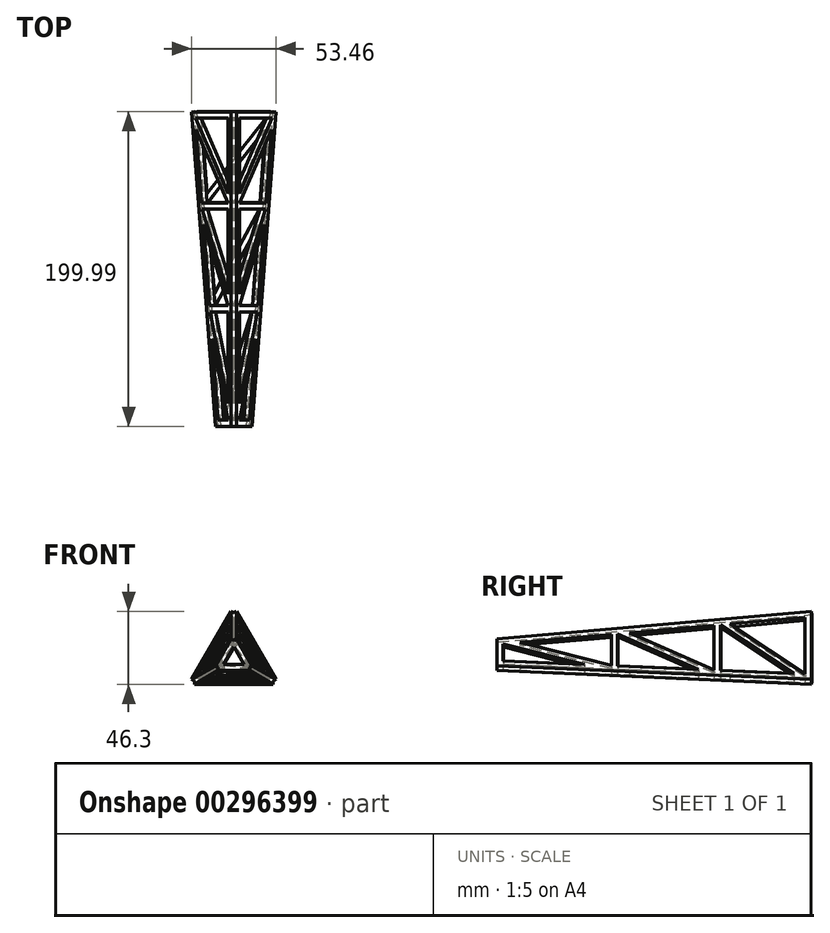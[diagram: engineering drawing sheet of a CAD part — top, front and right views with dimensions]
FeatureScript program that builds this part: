
annotation { "Feature Type Name" : "Feature", "Feature Type Description" : "" }
export const myFeature = defineFeature(function(context is Context, id is Id, definition is map)
    precondition{}
    {
        {
            assignVariable(context, id + "F0", {"name" : "thick", "anyValue" : 4});
        }
        {
            assignVariable(context, id + "F1", {"name" : "base", "anyValue" : 50});
        }
        {
            assignVariable(context, id + "F2", {"name" : "end", "anyValue" : 20});
        }
        {
            assignVariable(context, id + "F3", {"name" : "angleIn", "anyValue" : getVariable(context, 'base') / getVariable(context, 'end')});
        }
        {
            var Q0;
            Q0=qCreatedBy(makeId("Top.planeOp"),FACE);
            var sketch = newSketch(context, id + "F4", { "sketchPlane" : qUnion([Q0])});
            skLineSegment(sketch, "E0", {"start": v(0, 37.85) * mm, "end": v(0, -238.88) * mm, "construction": true});
            skSolve(sketch);
        }
        {
            var Q0;
            Q0=qCreatedBy(makeId("Front.planeOp"),FACE);
            var sketch = newSketch(context, id + "F5", { "sketchPlane" : qUnion([Q0])});
            skLineSegment(sketch, "E1", {"start": v(0, 0) * mm, "end": v(-25, 43.3) * mm, "construction": true});
            skLineSegment(sketch, "E2", {"start": v(0, 0) * mm, "end": v(-50, 0) * mm, "construction": true});
            skPoint(sketch, "E3", {"position": v(0, 0) * mm});
            skLineSegment(sketch, "E4", {"start": v(-25, 43.3) * mm, "end": v(-50, 0) * mm, "construction": true});
            skSolve(sketch);
        }
        {
            var Q0;
            Q0=qCreatedBy(makeId("Right.planeOp"),FACE);
            var sketch = newSketch(context, id + "F6", { "sketchPlane" : qUnion([Q0])});
            skLineSegment(sketch, "E5.0", {"start": v(-200, 35) * mm, "end": v(0, 50) * mm});
            skLineSegment(sketch, "E6.0.3", {"start": v(-200, 35) * mm, "end": v(-200, 15) * mm});
            skLineSegment(sketch, "E7.0", {"start": v(-200, 15) * mm, "end": v(0, 0) * mm});
            skLineSegment(sketch, "E8.0", {"start": v(0, 50) * mm, "end": v(0, 0) * mm});
            skLineSegment(sketch, "E9.0", {"start": v(-196, 31.29) * mm, "end": v(-4, 45.69) * mm});
            skLineSegment(sketch, "E9.1", {"start": v(-196, 31.29) * mm, "end": v(-196, 18.71) * mm});
            skLineSegment(sketch, "E9.2", {"start": v(-196, 18.71) * mm, "end": v(-4, 4.31) * mm});
            skLineSegment(sketch, "E9.3", {"start": v(-4, 45.69) * mm, "end": v(-4, 4.31) * mm});
            skLineSegment(sketch, "E10", {"start": v(-59.83, 8.5) * mm, "end": v(-59.83, 41.5) * mm, "construction": true});
            skLineSegment(sketch, "E11", {"start": v(-125.19, 36.6) * mm, "end": v(-125.19, 13.4) * mm, "construction": true});
            skLineSegment(sketch, "E12", {"start": v(0, 50) * mm, "end": v(-200, 50) * mm, "construction": true});
            skLineSegment(sketch, "E13", {"start": v(0, 0) * mm, "end": v(-200, 0) * mm, "construction": true});
            skLineSegment(sketch, "E14", {"start": v(-200, 0) * mm, "end": v(-200, 15) * mm, "construction": true});
            skLineSegment(sketch, "E15", {"start": v(-200, 50) * mm, "end": v(-200, 35) * mm, "construction": true});
            skLineSegment(sketch, "E16.0", {"start": v(-127.19, 36.45) * mm, "end": v(-127.19, 13.55) * mm});
            skLineSegment(sketch, "E17.0", {"start": v(-123.19, 36.75) * mm, "end": v(-123.19, 13.25) * mm});
            skLineSegment(sketch, "E18.0", {"start": v(-57.83, 8.35) * mm, "end": v(-57.83, 41.65) * mm});
            skLineSegment(sketch, "E19.0", {"start": v(-61.83, 8.65) * mm, "end": v(-61.83, 41.35) * mm});
            skLineSegment(sketch, "E20", {"start": v(-4, 4.31) * mm, "end": v(-51.93, 42.1) * mm});
            skLineSegment(sketch, "E21", {"start": v(-57.83, 41.65) * mm, "end": v(-11.14, 4.85) * mm});
            skLineSegment(sketch, "E22", {"start": v(-127.19, 13.55) * mm, "end": v(-185.34, 32.09) * mm});
            skLineSegment(sketch, "E23", {"start": v(-196, 31.29) * mm, "end": v(-144.4, 14.84) * mm});
            skLineSegment(sketch, "E24", {"start": v(-61.83, 8.65) * mm, "end": v(-115.72, 37.3) * mm});
            skLineSegment(sketch, "E25", {"start": v(-123.19, 36.75) * mm, "end": v(-71.75, 9.4) * mm});
            skSolve(sketch);
        }
        {
            var Q0;
            Q0=makeQuery(id+"F6.imprint","IMPRINT",FACE,{"disambiguationData":[TD([[makeQuery(id+"F6.imprint","IMPRINT",EDGE,{"derivedFrom":sQuery(id+"F6.wireOp",EDGE,"E5.0")}),-1.0]])]});
            var Q1;
            {var subQ0=sQuery(id+"F6.wireOp",EDGE,"E18.0");Q1=makeQuery(id+"F6.imprint","IMPRINT",FACE,{"disambiguationData":[TD([[makeQuery(id+"F6.imprint","IMPRINT",EDGE,{"derivedFrom":subQ0}),1.0]])]});}
            var Q2;
            {var subQ2=sQuery(id+"F6.wireOp",EDGE,"E24");Q2=makeQuery(id+"F6.imprint","IMPRINT",FACE,{"disambiguationData":[TD([[makeQuery(id+"F6.imprint","IMPRINT",EDGE,{"derivedFrom":subQ2}),1.0]])]});}
            var Q3;
            {var subQ0=sQuery(id+"F6.wireOp",EDGE,"E16.0");Q3=makeQuery(id+"F6.imprint","IMPRINT",FACE,{"disambiguationData":[TD([[makeQuery(id+"F6.imprint","IMPRINT",EDGE,{"derivedFrom":subQ0}),1.0]])]});}
            var Q4;
            {var subQ2=sQuery(id+"F6.wireOp",EDGE,"E22");Q4=makeQuery(id+"F6.imprint","IMPRINT",FACE,{"disambiguationData":[TD([[makeQuery(id+"F6.imprint","IMPRINT",EDGE,{"derivedFrom":subQ2}),1.0]])]});}
            var Q5;
            {var subQ2=sQuery(id+"F6.wireOp",EDGE,"E20");Q5=makeQuery(id+"F6.imprint","IMPRINT",FACE,{"disambiguationData":[TD([[makeQuery(id+"F6.imprint","IMPRINT",EDGE,{"derivedFrom":subQ2}),1.0]])]});}
            extrude(context, id + "F7", {"entities" : qUnion([Q0, Q1, Q2, Q3, Q4, Q5]), "endBound" : BoundingType.SYMMETRIC, "depth" : (getVariable(context, 'thick')) * mm});
        }
        {
            var Q0;
            Q0=makeQuery(id+"F7.opExtrude","SWEPT_BODY",BODY,{"disambiguationData":[OSD([sQuery(id+"F6.wireOp",EDGE,"E5.0"),sQuery(id+"F6.wireOp",EDGE,"E6.0.3"),sQuery(id+"F6.wireOp",EDGE,"E7.0"),sQuery(id+"F6.wireOp",EDGE,"E8.0"),sQuery(id+"F6.wireOp",EDGE,"E9.0"),sQuery(id+"F6.wireOp",EDGE,"E9.1"),sQuery(id+"F6.wireOp",EDGE,"E9.2"),sQuery(id+"F6.wireOp",EDGE,"E9.3"),sQuery(id+"F6.wireOp",EDGE,"E16.0"),sQuery(id+"F6.wireOp",EDGE,"E17.0"),sQuery(id+"F6.wireOp",EDGE,"E18.0"),sQuery(id+"F6.wireOp",EDGE,"E19.0"),sQuery(id+"F6.wireOp",EDGE,"E20"),sQuery(id+"F6.wireOp",EDGE,"E21"),sQuery(id+"F6.wireOp",EDGE,"E22"),sQuery(id+"F6.wireOp",EDGE,"E23"),sQuery(id+"F6.wireOp",EDGE,"E24"),sQuery(id+"F6.wireOp",EDGE,"E25")])]});
            var Q1;
            Q1=sQuery(id+"F4.wireOp",EDGE,"E0");
            transform(context, id + "F8", {"entities" : qUnion([Q0]), "transformType" : TransformType.ROTATION, "transformAxis" : qUnion([Q1]), "angle" : 30 * degree, "oppositeDirection" : true, "makeCopy" : true});
        }
        {
            var Q0;
            Q0=makeQuery(id+"F8.opPattern","COPY",BODY,{"derivedFrom":makeQuery(id+"F7.opExtrude","SWEPT_BODY",BODY,{"disambiguationData":[OSD([sQuery(id+"F6.wireOp",EDGE,"E5.0"),sQuery(id+"F6.wireOp",EDGE,"E6.0.3"),sQuery(id+"F6.wireOp",EDGE,"E7.0"),sQuery(id+"F6.wireOp",EDGE,"E8.0"),sQuery(id+"F6.wireOp",EDGE,"E9.0"),sQuery(id+"F6.wireOp",EDGE,"E9.1"),sQuery(id+"F6.wireOp",EDGE,"E9.2"),sQuery(id+"F6.wireOp",EDGE,"E9.3"),sQuery(id+"F6.wireOp",EDGE,"E16.0"),sQuery(id+"F6.wireOp",EDGE,"E17.0"),sQuery(id+"F6.wireOp",EDGE,"E18.0"),sQuery(id+"F6.wireOp",EDGE,"E19.0"),sQuery(id+"F6.wireOp",EDGE,"E20"),sQuery(id+"F6.wireOp",EDGE,"E21"),sQuery(id+"F6.wireOp",EDGE,"E22"),sQuery(id+"F6.wireOp",EDGE,"E23"),sQuery(id+"F6.wireOp",EDGE,"E24"),sQuery(id+"F6.wireOp",EDGE,"E25")])]}),"instanceName":"1"});
            transform(context, id + "F9", {"entities" : qUnion([Q0]), "transformType" : TransformType.TRANSLATION_3D, "dx" : (-(getVariable(context, 'base')) / (sqrt(3)) * sqrt(3)) * mm, "dy" : 0 * mm, "dz" : 0 * mm, "makeCopy" : false});
        }
        {
            var Q0;
            Q0=makeQuery(id+"F7.opExtrude","SWEPT_BODY",BODY,{"disambiguationData":[OSD([sQuery(id+"F6.wireOp",EDGE,"E5.0"),sQuery(id+"F6.wireOp",EDGE,"E6.0.3"),sQuery(id+"F6.wireOp",EDGE,"E7.0"),sQuery(id+"F6.wireOp",EDGE,"E8.0"),sQuery(id+"F6.wireOp",EDGE,"E9.0"),sQuery(id+"F6.wireOp",EDGE,"E9.1"),sQuery(id+"F6.wireOp",EDGE,"E9.2"),sQuery(id+"F6.wireOp",EDGE,"E9.3"),sQuery(id+"F6.wireOp",EDGE,"E16.0"),sQuery(id+"F6.wireOp",EDGE,"E17.0"),sQuery(id+"F6.wireOp",EDGE,"E18.0"),sQuery(id+"F6.wireOp",EDGE,"E19.0"),sQuery(id+"F6.wireOp",EDGE,"E20"),sQuery(id+"F6.wireOp",EDGE,"E21"),sQuery(id+"F6.wireOp",EDGE,"E22"),sQuery(id+"F6.wireOp",EDGE,"E23"),sQuery(id+"F6.wireOp",EDGE,"E24"),sQuery(id+"F6.wireOp",EDGE,"E25")])]});
            var Q1;
            Q1=sQuery(id+"F4.wireOp",EDGE,"E0");
            transform(context, id + "F10", {"entities" : qUnion([Q0]), "transformType" : TransformType.ROTATION, "transformAxis" : qUnion([Q1]), "angle" : 90 * degree, "makeCopy" : true});
        }
        {
            var Q0;
            Q0=makeQuery(id+"F7.opExtrude","SWEPT_BODY",BODY,{"disambiguationData":[OSD([sQuery(id+"F6.wireOp",EDGE,"E5.0"),sQuery(id+"F6.wireOp",EDGE,"E6.0.3"),sQuery(id+"F6.wireOp",EDGE,"E7.0"),sQuery(id+"F6.wireOp",EDGE,"E8.0"),sQuery(id+"F6.wireOp",EDGE,"E9.0"),sQuery(id+"F6.wireOp",EDGE,"E9.1"),sQuery(id+"F6.wireOp",EDGE,"E9.2"),sQuery(id+"F6.wireOp",EDGE,"E9.3"),sQuery(id+"F6.wireOp",EDGE,"E16.0"),sQuery(id+"F6.wireOp",EDGE,"E17.0"),sQuery(id+"F6.wireOp",EDGE,"E18.0"),sQuery(id+"F6.wireOp",EDGE,"E19.0"),sQuery(id+"F6.wireOp",EDGE,"E20"),sQuery(id+"F6.wireOp",EDGE,"E21"),sQuery(id+"F6.wireOp",EDGE,"E22"),sQuery(id+"F6.wireOp",EDGE,"E23"),sQuery(id+"F6.wireOp",EDGE,"E24"),sQuery(id+"F6.wireOp",EDGE,"E25")])]});
            var Q1;
            Q1=sQuery(id+"F4.wireOp",EDGE,"E0");
            transform(context, id + "F11", {"entities" : qUnion([Q0]), "transformType" : TransformType.ROTATION, "transformAxis" : qUnion([Q1]), "angle" : 30 * degree, "makeCopy" : false});
        }
        {
            var Q0;
            Q0=makeQuery(id+"F7.opExtrude","SWEPT_BODY",BODY,{"disambiguationData":[OSD([sQuery(id+"F6.wireOp",EDGE,"E5.0"),sQuery(id+"F6.wireOp",EDGE,"E6.0.3"),sQuery(id+"F6.wireOp",EDGE,"E7.0"),sQuery(id+"F6.wireOp",EDGE,"E8.0"),sQuery(id+"F6.wireOp",EDGE,"E9.0"),sQuery(id+"F6.wireOp",EDGE,"E9.1"),sQuery(id+"F6.wireOp",EDGE,"E9.2"),sQuery(id+"F6.wireOp",EDGE,"E9.3"),sQuery(id+"F6.wireOp",EDGE,"E16.0"),sQuery(id+"F6.wireOp",EDGE,"E17.0"),sQuery(id+"F6.wireOp",EDGE,"E18.0"),sQuery(id+"F6.wireOp",EDGE,"E19.0"),sQuery(id+"F6.wireOp",EDGE,"E20"),sQuery(id+"F6.wireOp",EDGE,"E21"),sQuery(id+"F6.wireOp",EDGE,"E22"),sQuery(id+"F6.wireOp",EDGE,"E23"),sQuery(id+"F6.wireOp",EDGE,"E24"),sQuery(id+"F6.wireOp",EDGE,"E25")])]});
            var Q1;
            Q1=sQuery(id+"F5.wireOp",EDGE,"E1");
            transform(context, id + "F12", {"entities" : qUnion([Q0]), "transformType" : TransformType.ROTATION, "transformAxis" : qUnion([Q1]), "angle" : (getVariable(context, 'angleIn')) * degree, "oppositeDirection" : true, "makeCopy" : false});
        }
        {
            var Q0;
            Q0=makeQuery(id+"F8.opPattern","COPY",BODY,{"derivedFrom":makeQuery(id+"F7.opExtrude","SWEPT_BODY",BODY,{"disambiguationData":[OSD([sQuery(id+"F6.wireOp",EDGE,"E5.0"),sQuery(id+"F6.wireOp",EDGE,"E6.0.3"),sQuery(id+"F6.wireOp",EDGE,"E7.0"),sQuery(id+"F6.wireOp",EDGE,"E8.0"),sQuery(id+"F6.wireOp",EDGE,"E9.0"),sQuery(id+"F6.wireOp",EDGE,"E9.1"),sQuery(id+"F6.wireOp",EDGE,"E9.2"),sQuery(id+"F6.wireOp",EDGE,"E9.3"),sQuery(id+"F6.wireOp",EDGE,"E16.0"),sQuery(id+"F6.wireOp",EDGE,"E17.0"),sQuery(id+"F6.wireOp",EDGE,"E18.0"),sQuery(id+"F6.wireOp",EDGE,"E19.0"),sQuery(id+"F6.wireOp",EDGE,"E20"),sQuery(id+"F6.wireOp",EDGE,"E21"),sQuery(id+"F6.wireOp",EDGE,"E22"),sQuery(id+"F6.wireOp",EDGE,"E23"),sQuery(id+"F6.wireOp",EDGE,"E24"),sQuery(id+"F6.wireOp",EDGE,"E25")])]}),"instanceName":"1"});
            var Q1;
            Q1=sQuery(id+"F5.wireOp",EDGE,"E4");
            transform(context, id + "F13", {"entities" : qUnion([Q0]), "transformType" : TransformType.ROTATION, "transformAxis" : qUnion([Q1]), "angle" : (getVariable(context, 'angleIn')) * degree, "oppositeDirection" : true, "makeCopy" : false});
        }
        {
            var Q0;
            Q0=makeQuery(id+"F10.opPattern","COPY",BODY,{"derivedFrom":makeQuery(id+"F7.opExtrude","SWEPT_BODY",BODY,{"disambiguationData":[OSD([sQuery(id+"F6.wireOp",EDGE,"E5.0"),sQuery(id+"F6.wireOp",EDGE,"E6.0.3"),sQuery(id+"F6.wireOp",EDGE,"E7.0"),sQuery(id+"F6.wireOp",EDGE,"E8.0"),sQuery(id+"F6.wireOp",EDGE,"E9.0"),sQuery(id+"F6.wireOp",EDGE,"E9.1"),sQuery(id+"F6.wireOp",EDGE,"E9.2"),sQuery(id+"F6.wireOp",EDGE,"E9.3"),sQuery(id+"F6.wireOp",EDGE,"E16.0"),sQuery(id+"F6.wireOp",EDGE,"E17.0"),sQuery(id+"F6.wireOp",EDGE,"E18.0"),sQuery(id+"F6.wireOp",EDGE,"E19.0"),sQuery(id+"F6.wireOp",EDGE,"E20"),sQuery(id+"F6.wireOp",EDGE,"E21"),sQuery(id+"F6.wireOp",EDGE,"E22"),sQuery(id+"F6.wireOp",EDGE,"E23"),sQuery(id+"F6.wireOp",EDGE,"E24"),sQuery(id+"F6.wireOp",EDGE,"E25")])]}),"instanceName":"1"});
            var Q1;
            Q1=sQuery(id+"F5.wireOp",EDGE,"E2");
            transform(context, id + "F14", {"entities" : qUnion([Q0]), "transformType" : TransformType.ROTATION, "transformAxis" : qUnion([Q1]), "angle" : (getVariable(context, 'angleIn')) * degree, "makeCopy" : false});
        }
    });
